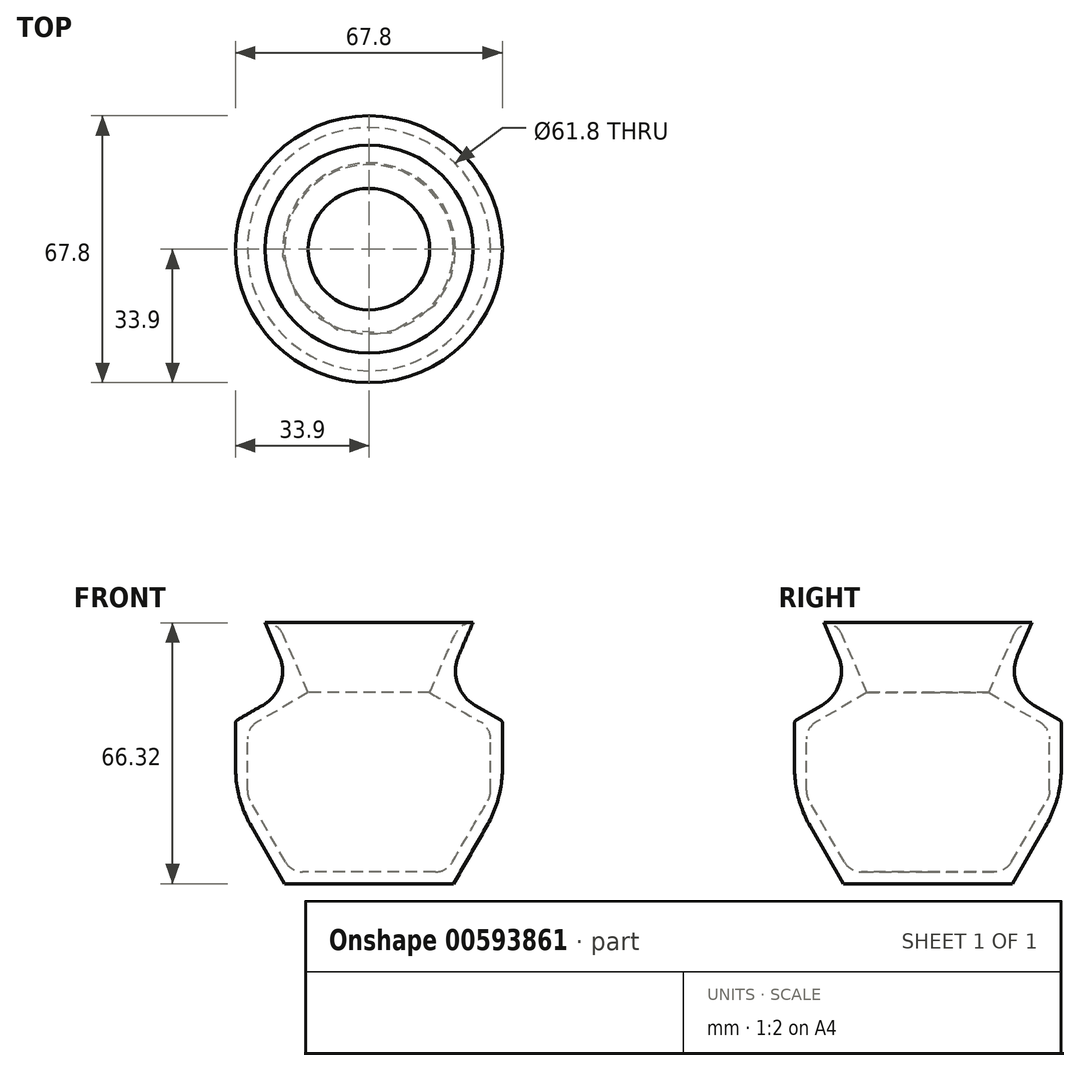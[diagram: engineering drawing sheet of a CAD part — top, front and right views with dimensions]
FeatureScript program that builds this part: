
annotation { "Feature Type Name" : "Feature", "Feature Type Description" : "" }
export const myFeature = defineFeature(function(context is Context, id is Id, definition is map)
    precondition{}
    {
        {
            var Q0;
            Q0=qCreatedBy(makeId("Front.planeOp"),FACE);
            var sketch = newSketch(context, id + "F0", { "sketchPlane" : qUnion([Q0])});
            skLineSegment(sketch, "E0", {"start": v(0, -24.74) * mm, "end": v(21.48, -24.74) * mm});
            skLineSegment(sketch, "E1", {"start": v(21.48, -24.74) * mm, "end": v(33.9, -3.23) * mm});
            skLineSegment(sketch, "E2", {"start": v(33.9, -3.23) * mm, "end": v(33.9, 16.62) * mm});
            skLineSegment(sketch, "E3", {"start": v(33.9, 16.62) * mm, "end": v(19.25, 25.08) * mm});
            skLineSegment(sketch, "E4", {"start": v(19.25, 25.08) * mm, "end": v(26.4, 41.58) * mm});
            skLineSegment(sketch, "E5.0", {"start": v(15.44, 23.81) * mm, "end": v(23.65, 42.78) * mm});
            skLineSegment(sketch, "E5.1", {"start": v(0, -21.74) * mm, "end": v(16.86, -21.74) * mm});
            skLineSegment(sketch, "E5.2", {"start": v(21.19, -19.24) * mm, "end": v(30.23, -3.58) * mm});
            skLineSegment(sketch, "E5.3", {"start": v(30.9, -1.08) * mm, "end": v(30.9, 12) * mm});
            skLineSegment(sketch, "E5.4", {"start": v(28.4, 16.33) * mm, "end": v(15.44, 23.81) * mm});
            skLineSegment(sketch, "E6", {"start": v(23.65, 42.78) * mm, "end": v(26.4, 41.58) * mm});
            skLineSegment(sketch, "E7", {"start": v(0, -21.74) * mm, "end": v(0, -24.74) * mm});
            skLineSegment(sketch, "E8", {"start": v(0, 57.6) * mm, "end": v(0, -44.53) * mm, "construction": true});
            skPoint(sketch, "E9.visualSharp", {"position": v(30.9, 14.89) * mm});
            skArc(sketch, "E9.filletArc", {"start": v(30.9, 12) * mm, "mid": v(30.23, 14.5) * mm, "end": v(28.4, 16.33) * mm});
            skPoint(sketch, "E10.visualSharp", {"position": v(30.9, -2.42) * mm});
            skArc(sketch, "E10.filletArc", {"start": v(30.23, -3.58) * mm, "mid": v(30.73, -2.38) * mm, "end": v(30.9, -1.08) * mm});
            skPoint(sketch, "E11.visualSharp", {"position": v(19.75, -21.74) * mm});
            skArc(sketch, "E11.filletArc", {"start": v(16.86, -21.74) * mm, "mid": v(19.36, -21.07) * mm, "end": v(21.19, -19.24) * mm});
            skSolve(sketch);
        }
        {
            var Q0;
            Q0=makeQuery(id+"F0.imprint","IMPRINT",FACE,{"disambiguationData":[TD([[makeQuery(id+"F0.imprint","IMPRINT",EDGE,{"derivedFrom":sQuery(id+"F0.wireOp",EDGE,"E0")}),1.0]])]});
            var Q1;
            Q1=sQuery(id+"F0.wireOp",EDGE,"E8");
            revolve(context, id + "F1", {"entities" : qUnion([Q0]), "axis" : qUnion([Q1]), "revolveType" : RevolveType.FULL});
        }
        {
            var Q0;
            Q0=makeQuery(id+"F1.opRevolve","SWEPT_EDGE",EDGE,{"disambiguationData":[OSD([sQuery(id+"F0.wireOp",EDGE,"E1"),sQuery(id+"F0.wireOp",EDGE,"E2")])]});
            fillet(context, id + "F2", {"entities" : qUnion([Q0]), "radius" : 30 * mm, "tangentPropagation" : true, "allowEdgeOverflow" : false});
        }
        {
            var Q0;
            Q0=makeQuery(id+"F1.opRevolve","SWEPT_EDGE",EDGE,{"disambiguationData":[OSD([sQuery(id+"F0.wireOp",EDGE,"E3"),sQuery(id+"F0.wireOp",EDGE,"E4")])]});
            fillet(context, id + "F3", {"entities" : qUnion([Q0]), "radius" : 10 * mm, "allowEdgeOverflow" : false});
        }
        {
            var Q0;
            Q0=makeQuery(id+"F1.opRevolve","SWEPT_EDGE",EDGE,{"disambiguationData":[OSD([sQuery(id+"F0.wireOp",EDGE,"E2"),sQuery(id+"F0.wireOp",EDGE,"E3")])]});
            fillet(context, id + "F4", {"entities" : qUnion([Q0]), "radius" : 1 * mm, "tangentPropagation" : true, "allowEdgeOverflow" : false});
        }
        {
            var Q0;
            Q0=makeQuery(id+"F1.opRevolve","SWEPT_EDGE",EDGE,{"disambiguationData":[OSD([sQuery(id+"F0.wireOp",EDGE,"E5.0"),sQuery(id+"F0.wireOp",EDGE,"E6")])]});
            fillet(context, id + "F5", {"entities" : qUnion([Q0]), "radius" : 5 * mm, "tangentPropagation" : true, "allowEdgeOverflow" : false});
        }
    });
